# Revit family: FTTO Netzteil MS700741
name_source: partatom
category: Datengeräte
units: mm (PartAtom-declared; Revit-internal decimal feet)

## family parameters
Arbeitsebenenbasiert = Nein
Beim Laden mit Abzugskörper schneiden = Nein
Bemaßung runder Anschluss = Durchmesser verwenden
Beschriftungsausrichtung beibehalten = Nein
Gemeinsam genutzt = Nein
Immer vertikal = Ja
OmniClass-Nummer = 23.85.50.17
OmniClass-Titel = Communication and Data Processing Equipment
Raumberechnungspunkt = Nein
Teiletyp = Normal

## types (1)
- FTTO Netzteil MS700741
    Artikelnummer = MS700741
    Beschreibung = Installationsnetzteil PoE+ 65W
    Eigenschaft 1 = 1m Zuleitung
    Eigenschaft 2 = Combicon-Stecker
    Eigenschaft 3 = offen 3 x1,5 mm²
    Hersteller = MICROSENS
    Leistung = 65W
    Spannung Primär = 115..230VAC
    Spannung Sekundär = 54 VDC/1,2A
    Vorgabe-Ansicht = 0 mm  [stored 0 ft]

note: [stored X ft] marks values corroborated as IEEE doubles in the binary element streams (Revit-internal decimal feet)
